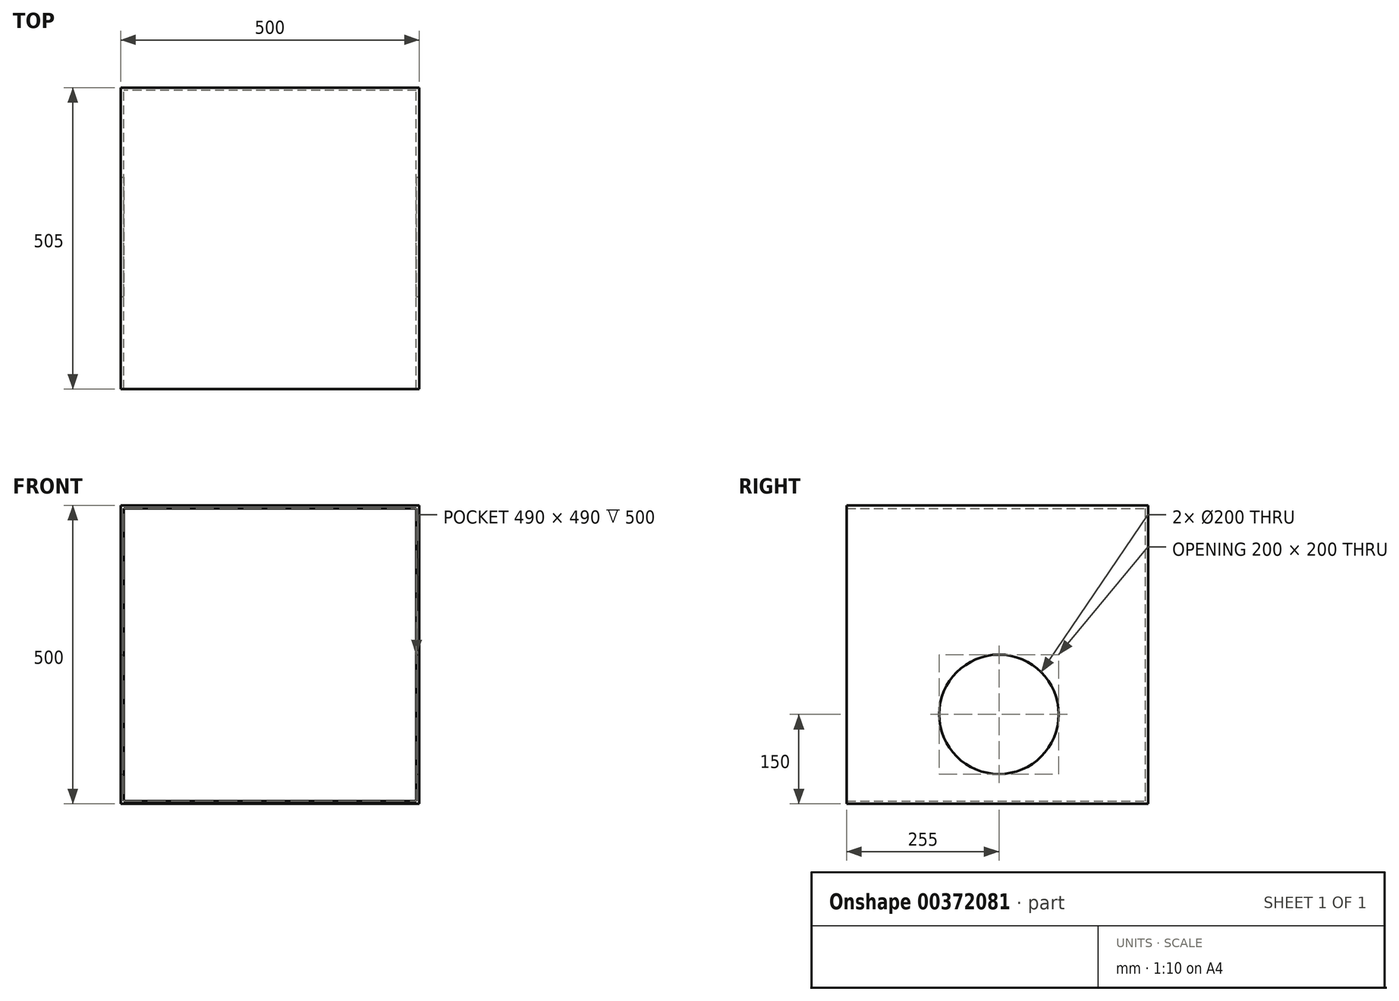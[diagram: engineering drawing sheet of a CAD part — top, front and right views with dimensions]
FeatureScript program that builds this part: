
annotation { "Feature Type Name" : "Feature", "Feature Type Description" : "" }
export const myFeature = defineFeature(function(context is Context, id is Id, definition is map)
    precondition{}
    {
        {
            var Q0;
            Q0=qCreatedBy(makeId("Top.planeOp"),FACE);
            var sketch = newSketch(context, id + "F0", { "sketchPlane" : qUnion([Q0])});
            skLineSegment(sketch, "E0.bottom", {"start": v(250, -2.5) * mm, "end": v(-250, -2.5) * mm});
            skLineSegment(sketch, "E0.top", {"start": v(250, 2.5) * mm, "end": v(-250, 2.5) * mm});
            skLineSegment(sketch, "E0.left", {"start": v(250, -2.5) * mm, "end": v(250, 2.5) * mm});
            skLineSegment(sketch, "E0.right", {"start": v(-250, -2.5) * mm, "end": v(-250, 2.5) * mm});
            skPoint(sketch, "E0.middle", {"position": v(0, 0) * mm});
            skSolve(sketch);
        }
        {
            var Q0;
            Q0 = qSketchRegion(id + "F0", true);
            extrude(context, id + "F1", {"entities" : qUnion([Q0]), "depth" : 500 * mm});
        }
        {
            var Q0;
            Q0=makeQuery(id+"F1.opExtrude","SWEPT_FACE",FACE,{"disambiguationData":[OSD([sQuery(id+"F0.wireOp",EDGE,"E0.bottom")])]});
            var sketch = newSketch(context, id + "F2", { "sketchPlane" : qUnion([Q0])});
            skLineSegment(sketch, "E1.0", {"start": v(250, 500) * mm, "end": v(-250, 500) * mm});
            skLineSegment(sketch, "E2.0", {"start": v(250, 495) * mm, "end": v(-250, 495) * mm});
            skLineSegment(sketch, "E3", {"start": v(-250, 500) * mm, "end": v(-250, 495) * mm});
            skLineSegment(sketch, "E4", {"start": v(250, 500) * mm, "end": v(250, 495) * mm});
            skSolve(sketch);
        }
        {
            var Q0;
            Q0=makeQuery(id+"F2.imprint","IMPRINT",FACE,{"disambiguationData":[TD([[makeQuery(id+"F2.imprint","IMPRINT",EDGE,{"derivedFrom":sQuery(id+"F2.wireOp",EDGE,"E1.0")}),1.0]])]});
            extrude(context, id + "F3", {"entities" : qUnion([Q0]), "operationType" : NewBodyOperationType.ADD, "depth" : 500 * mm});
        }
        {
            var Q0;
            Q0=makeQuery(id+"F1.opExtrude","SWEPT_FACE",FACE,{"disambiguationData":[OSD([sQuery(id+"F0.wireOp",EDGE,"E0.bottom")])]});
            var sketch = newSketch(context, id + "F4", { "sketchPlane" : qUnion([Q0])});
            skLineSegment(sketch, "E5.0", {"start": v(250, 0) * mm, "end": v(-250, 0) * mm});
            skLineSegment(sketch, "E6.0", {"start": v(250, 5) * mm, "end": v(-250, 5) * mm});
            skLineSegment(sketch, "E7", {"start": v(250, 5) * mm, "end": v(250, 0) * mm});
            skLineSegment(sketch, "E8", {"start": v(-250, 5) * mm, "end": v(-250, 0) * mm});
            skSolve(sketch);
        }
        {
            var Q0;
            Q0 = qSketchRegion(id + "F4", true);
            extrude(context, id + "F5", {"entities" : qUnion([Q0]), "operationType" : NewBodyOperationType.ADD, "depth" : 500 * mm});
        }
        {
            var Q0;
            Q0=makeQuery(id+"F1.opExtrude","SWEPT_FACE",FACE,{"disambiguationData":[OSD([sQuery(id+"F0.wireOp",EDGE,"E0.bottom")])]});
            var sketch = newSketch(context, id + "F6", { "sketchPlane" : qUnion([Q0])});
            skLineSegment(sketch, "E9.0", {"start": v(250, 495) * mm, "end": v(250, 5) * mm});
            skLineSegment(sketch, "E10.0", {"start": v(-250, 495) * mm, "end": v(-250, 5) * mm});
            skLineSegment(sketch, "E11.0", {"start": v(245, 495) * mm, "end": v(245, 5) * mm});
            skLineSegment(sketch, "E12.0", {"start": v(-245, 495) * mm, "end": v(-245, 5) * mm});
            skLineSegment(sketch, "E13", {"start": v(250, 5) * mm, "end": v(245, 5) * mm});
            skLineSegment(sketch, "E14", {"start": v(-245, 5) * mm, "end": v(-250, 5) * mm});
            skLineSegment(sketch, "E15", {"start": v(-245, 495) * mm, "end": v(-250, 495) * mm});
            skLineSegment(sketch, "E16", {"start": v(250, 495) * mm, "end": v(245, 495) * mm});
            skSolve(sketch);
        }
        {
            var Q0;
            Q0 = qSketchRegion(id + "F6", true);
            extrude(context, id + "F7", {"entities" : qUnion([Q0]), "operationType" : NewBodyOperationType.ADD, "depth" : 500 * mm});
        }
        {
            var Q0;
            Q0=qCreatedBy(makeId("Right.planeOp"),FACE);
            var sketch = newSketch(context, id + "F8", { "sketchPlane" : qUnion([Q0])});
            skCircle(sketch, "E17", {"center": v(-247.5, 150) * mm, "radius": 100 * mm});
            skSolve(sketch);
        }
        {
            var Q0;
            Q0 = qSketchRegion(id + "F8", true);
            extrude(context, id + "F9", {"entities" : qUnion([Q0]), "operationType" : NewBodyOperationType.REMOVE, "endBound" : BoundingType.SYMMETRIC, "oppositeDirection" : true, "depth" : 602 * mm});
        }
    });
